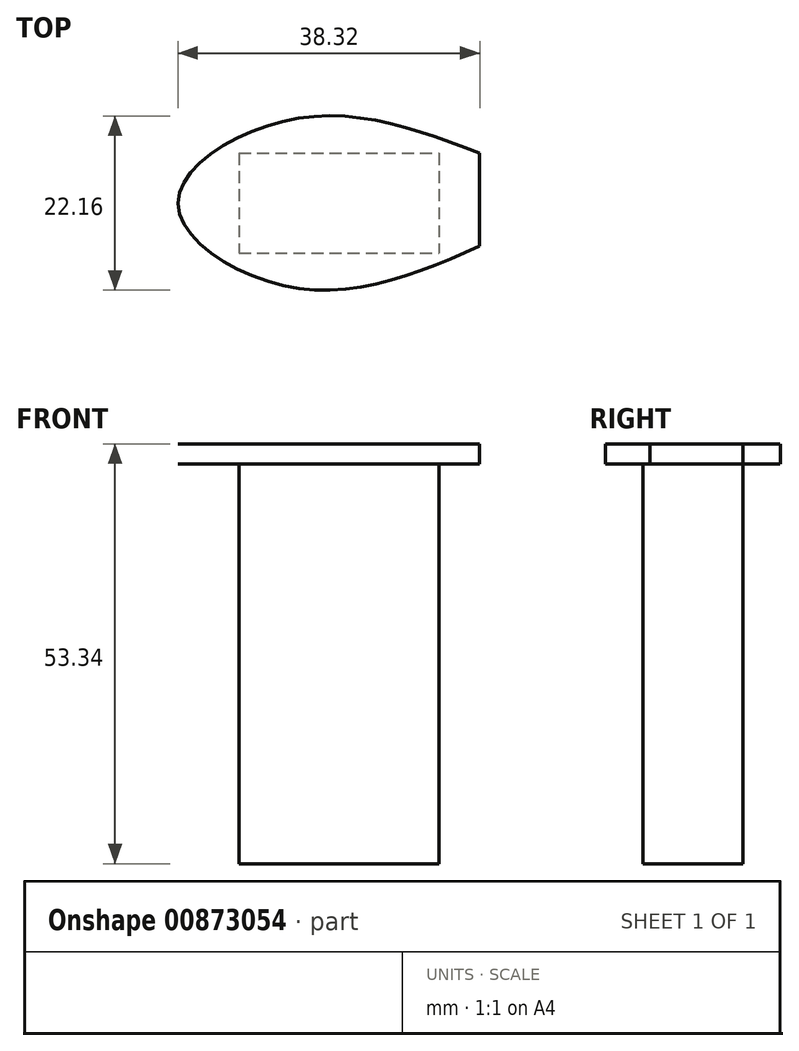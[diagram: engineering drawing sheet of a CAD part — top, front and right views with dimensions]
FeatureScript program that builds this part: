
annotation { "Feature Type Name" : "Feature", "Feature Type Description" : "" }
export const myFeature = defineFeature(function(context is Context, id is Id, definition is map)
    precondition{}
    {
        {
            var Q0;
            Q0=qCreatedBy(makeId("Top.planeOp"),FACE);
            var sketch = newSketch(context, id + "F0", { "sketchPlane" : qUnion([Q0])});
            skLineSegment(sketch, "E0.bottom", {"start": v(-8.72, 15.36) * mm, "end": v(16.68, 15.36) * mm});
            skLineSegment(sketch, "E0.top", {"start": v(-8.72, 2.66) * mm, "end": v(16.68, 2.66) * mm});
            skLineSegment(sketch, "E0.left", {"start": v(-8.72, 15.36) * mm, "end": v(-8.72, 2.66) * mm});
            skLineSegment(sketch, "E0.right", {"start": v(16.68, 15.36) * mm, "end": v(16.68, 2.66) * mm});
            skSolve(sketch);
        }
        {
            var Q0;
            Q0 = qSketchRegion(id + "F0", true);
            extrude(context, id + "F1", {"entities" : qUnion([Q0]), "depth" : 50.8 * mm, "offsetDistance" : 25.4 * mm});
        }
        {
            var Q0;
            Q0=makeQuery(id+"F1.opExtrude","CAP_FACE",FACE,{"disambiguationData":[OSD([sQuery(id+"F0.wireOp",EDGE,"E0.bottom"),sQuery(id+"F0.wireOp",EDGE,"E0.top"),sQuery(id+"F0.wireOp",EDGE,"E0.left"),sQuery(id+"F0.wireOp",EDGE,"E0.right")])],"isStart":false});
            var sketch = newSketch(context, id + "F2", { "sketchPlane" : qUnion([Q0])});
            skLineSegment(sketch, "E1.left", {"start": v(-16.47, 8.98) * mm, "end": v(-16.47, 8.96) * mm});
            skLineSegment(sketch, "E1.right", {"start": v(21.85, 15.36) * mm, "end": v(21.85, 3.52) * mm});
            skFitSpline(sketch, "E2", {"points": [v(21.85, 15.36) * mm, v(-1.83, 19.67) * mm, v(-16.47, 8.96) * mm, v(-1.72, -1.75) * mm, v(21.85, 3.52) * mm], "startDerivative": vector(-86.7, 32.7) * mm, "endDerivative": vector(85.9, 37.33) * mm});
            skPoint(sketch, "E3.orphan", {"position": v(-16.47, 19.67) * mm});
            skPoint(sketch, "E4.orphan", {"position": v(-16.47, -1.75) * mm});
            skSolve(sketch);
        }
        {
            var Q0;
            Q0 = qSketchRegion(id + "F2", true);
            extrude(context, id + "F3", {"entities" : qUnion([Q0]), "operationType" : NewBodyOperationType.ADD, "depth" : 2.54 * mm, "offsetDistance" : 25.4 * mm});
        }
    });
